# Revit family: Allwood_side_chair_AV35 R1
name_source: partatom
category: Furniture
units: mm (PartAtom-declared; Revit-internal decimal feet)

## family parameters
Always vertical = Yes
Cut with Voids When Loaded = No
Enable Cutting in Views = No
OmniClass Number = 23.40.20.00
OmniClass Title = General Furniture and Specialties
Render Appearance Source = Family Geometry
Room Calculation Point = No
Shared = No
Work Plane-Based = No

## types (1)
- Allwood_side_chair_AV35 R1
    Default Elevation = 0 mm  [stored 0 ft]
    Depth = 50cm/19,7in
    Design = Anderssen & Voll
    Design Year = 2024
    Frame and seat = &tradition Lacquered Oak Horizontal
    Height = 79cm/31,1in
    Manufacturer = &Tradition
    Model = AV35 Allwood
    Packaging dimensions & weight = Please see product fact sheet available from download page on website
    Type Comments = Allwood
    URL = https://www.andtradition.com
    Variation = Please visit our website to see available colours and finishes.
    Width = 48cm/18,9in

note: [stored X ft] marks values corroborated as IEEE doubles in the binary element streams (Revit-internal decimal feet)

## geometry (parser evidence)
native form markers: Sweep x1
no freeform markers — native parametric forms only
